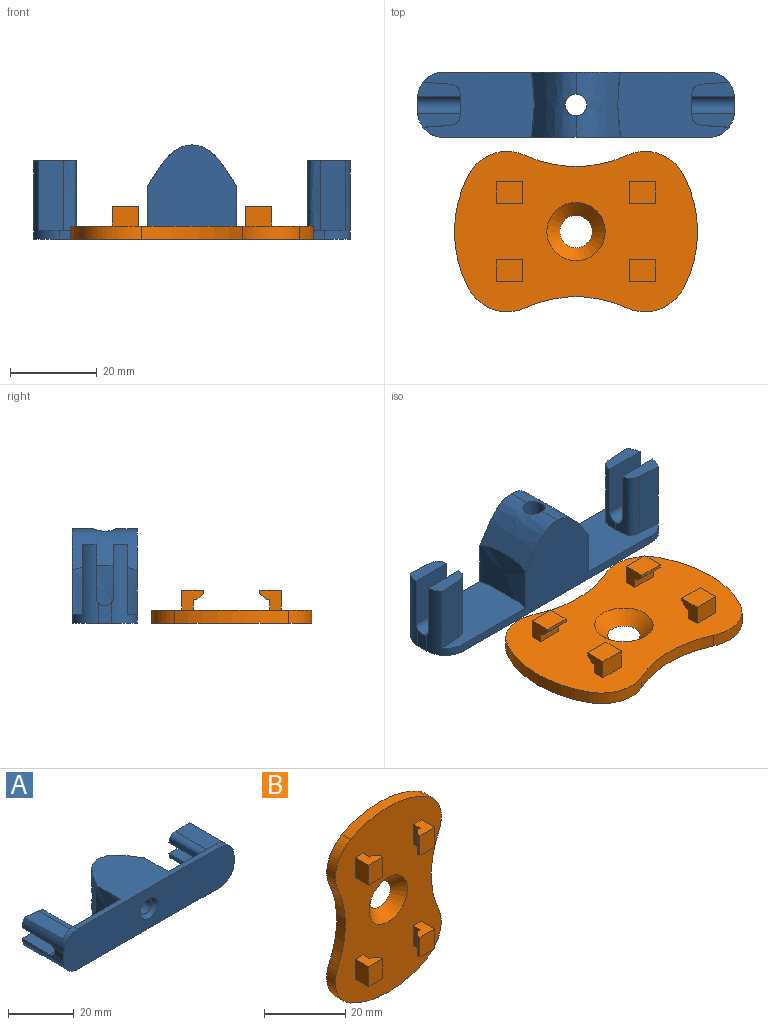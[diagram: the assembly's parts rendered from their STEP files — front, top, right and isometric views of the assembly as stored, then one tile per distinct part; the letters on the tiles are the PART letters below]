
ASSEMBLY  parts=2 mates=1
PART A: 35 faces, bbox 73x21.7x15 mm
  f0: plane 9.98x3.3mm, normal (0,1,0), area 26.2mm2, adj f14,f15,f26,f31
  f1: plane 9.98x3.3mm, normal (0,1,0), area 26.2mm2, adj f19,f20,f27,f29
  f2: extruded ~15x10.29mm, area 195.9mm2, adj f3,f7,f9,f22,f23
  f3: extruded ~15x10.29mm, area 195.9mm2, adj f2,f4,f7,f9,f23
  f4: extruded ~15x11.24mm, area 165.3mm2, adj f3,f5,f7,f9
  f5: plane 25.71x15mm, normal (0,1,0), area 293.2mm2, adj f4,f7,f9,f17,f18,f19,f20,f27
  f6: plane 4.68x3mm, normal (-1,0,0), area 12.6mm2, adj f10,f25,f26,f33
  f7: plane 61x21.71mm, normal (0,0,-1), area 460.3mm2, adj f2,f3,f4,f5,f10,f11,f22,f25
  f8: plane 4.68x3mm, normal (1,0,0), area 12.6mm2, adj f10,f27,f28,f34
  f9: plane 61x21.71mm, normal (0,0,1), area 461mm2, adj f2,f3,f4,f5,f10,f11,f22,f26
  f10: plane 73x15mm, normal (0,-1,0), area 1020.6mm2, adj f6,f7,f8,f9,f24,f25,f26,f27
  f11: plane 25.71x15mm, normal (0,1,0), area 293.2mm2, adj f7,f9,f12,f13,f14,f15,f22,f25
  f12: plane 16x5.75mm, normal (0.06,0,-1), area 92.2mm2, adj f11,f13,f16,f25
  f13: extruded ~16x4.79mm, area 77.9mm2, adj f11,f12,f14,f16,f32,f33
  f14: extruded ~16x4.79mm, area 77.9mm2, adj f0,f11,f13,f15,f31,f33
  f15: plane 16x5.75mm, normal (0.06,0,1), area 92.2mm2, adj f0,f11,f14,f26
  f16: plane 9.98x3.3mm, normal (0,1,0), area 26.2mm2, adj f12,f13,f25,f32
  f17: plane 16x5.75mm, normal (-0.06,0,1), area 92.2mm2, adj f5,f18,f21,f28
  f18: extruded ~16x4.79mm, area 77.9mm2, adj f5,f17,f19,f21,f30,f34
  f19: extruded ~16x4.79mm, area 77.9mm2, adj f1,f5,f18,f20,f29,f34
  f20: plane 16x5.75mm, normal (-0.06,0,-1), area 92.2mm2, adj f1,f5,f19,f27
  f21: plane 9.98x3.3mm, normal (0,1,0), area 26.2mm2, adj f17,f18,f28,f30
  f22: extruded ~15x11.24mm, area 165.3mm2, adj f2,f7,f9,f11
  f23: cylinder r=2.5mm len=20.49mm, axis (0,-1,0), area 317.3mm2, adj f2,f3,f24
  f24: cone r=2.5mm half-angle=45deg, axis (0,-1,0), area 33.7mm2, adj f10,f23
  f25: cylinder r=6mm len=18mm, axis (0,-1,0), area 75.5mm2, adj f6,f7,f10,f11,f12,f16,f32,f33
  f26: cylinder r=6mm len=18mm, axis (0,1,0), area 75.5mm2, adj f0,f6,f9,f10,f11,f15,f31,f33
  f27: cylinder r=6mm len=18mm, axis (0,-1,0), area 75.5mm2, adj f1,f5,f7,f8,f10,f20,f29,f34
  f28: cylinder r=6mm len=18mm, axis (0,1,0), area 75.5mm2, adj f5,f8,f9,f10,f17,f21,f30,f34
  f29: plane 12x9.88mm, normal (0,0,1), area 118.5mm2, adj f1,f19,f27,f34
  f30: plane 12x9.88mm, normal (0,0,-1), area 118.5mm2, adj f18,f21,f28,f34
  f31: plane 12x9.88mm, normal (0,0,-1), area 118.5mm2, adj f0,f14,f26,f33
  f32: plane 12x9.88mm, normal (0,0,1), area 118.5mm2, adj f13,f16,f25,f33
  f33: cylinder r=2mm len=10mm, axis (-1,0,0), area 62.5mm2, adj f6,f13,f14,f25,f26,f31,f32
  f34: cylinder r=2mm len=10mm, axis (1,0,0), area 62.5mm2, adj f8,f18,f19,f27,f28,f29,f30
PART B: 43 faces, bbox 37x7.6x56 mm
  f0: plane 6x2.36mm, normal (-1,0,0), area 14.2mm2, adj f4,f22,f24,f32
  f1: plane 6x2.36mm, normal (-1,0,0), area 14.2mm2, adj f4,f18,f20,f30
  f2: plane 6x2.36mm, normal (1,0,0), area 14.2mm2, adj f4,f14,f16,f28
  f3: plane 6x2.36mm, normal (1,0,0), area 14.2mm2, adj f4,f10,f11,f26
  f4: plane 56x36.95mm, normal (0,-1,0), area 1554.1mm2, adj f0,f1,f2,f3,f5,f6,f7,f8
  f5: cylinder r=28mm len=23.4mm, axis (0,-1,0), area 72.4mm2, adj f4,f9,f35,f38
  f6: cylinder r=28mm len=26.37mm, axis (0,-1,0), area 82.4mm2, adj f4,f9,f35,f36
  f7: cylinder r=28mm len=23.4mm, axis (0,-1,0), area 72.4mm2, adj f4,f9,f36,f37
  f8: cylinder r=28mm len=26.37mm, axis (0,-1,0), area 82.4mm2, adj f4,f9,f37,f38
  f9: plane 56x36.95mm, normal (0,1,0), area 1717.3mm2, adj f5,f6,f7,f8,f34,f35,f36,f37
  f10: plane 5x4.56mm, normal (0,0,-1), area 16.2mm2, adj f3,f4,f12,f13,f26,f27,f41
  f11: plane 5x4.56mm, normal (0,0,1), area 16.2mm2, adj f3,f4,f12,f13,f26,f27,f41
  f12: plane 6x4.56mm, normal (-1,0,0), area 27.4mm2, adj f4,f10,f11,f13
  f13: plane 6x5mm, normal (0,-1,0), area 30mm2, adj f10,f11,f12,f27
  f14: plane 5x4.56mm, normal (0,0,1), area 16.2mm2, adj f2,f4,f15,f17,f28,f29,f42
  f15: plane 6x4.56mm, normal (-1,0,0), area 27.4mm2, adj f4,f14,f16,f17
  f16: plane 5x4.56mm, normal (0,0,-1), area 16.2mm2, adj f2,f4,f15,f17,f28,f29,f42
  f17: plane 6x5mm, normal (0,-1,0), area 30mm2, adj f14,f15,f16,f29
  f18: plane 5x4.56mm, normal (0,0,-1), area 16.2mm2, adj f1,f4,f19,f21,f30,f31,f39
  f19: plane 6x4.56mm, normal (1,0,0), area 27.4mm2, adj f4,f18,f20,f21
  f20: plane 5x4.56mm, normal (0,0,1), area 16.2mm2, adj f1,f4,f19,f21,f30,f31,f39
  f21: plane 6x5mm, normal (0,-1,0), area 30mm2, adj f18,f19,f20,f31
  f22: plane 5x4.56mm, normal (0,0,-1), area 16.2mm2, adj f0,f4,f23,f25,f32,f33,f40
  f23: plane 6x4.56mm, normal (1,0,0), area 27.4mm2, adj f4,f22,f24,f25
  f24: plane 5x4.56mm, normal (0,0,1), area 16.2mm2, adj f0,f4,f23,f25,f32,f33,f40
  f25: plane 6x5mm, normal (0,-1,0), area 30mm2, adj f22,f23,f24,f33
  f26: plane 6x0.8mm, normal (0,1,0), area 4.8mm2, adj f3,f10,f11,f41
  f27: plane 6x0.7mm, normal (1,0,0), area 4.2mm2, adj f10,f11,f13,f41
  f28: plane 6x0.8mm, normal (0,1,0), area 4.8mm2, adj f2,f14,f16,f42
  f29: plane 6x0.7mm, normal (1,0,0), area 4.2mm2, adj f14,f16,f17,f42
  f30: plane 6x0.8mm, normal (0,1,0), area 4.8mm2, adj f1,f18,f20,f39
  f31: plane 6x0.7mm, normal (-1,0,0), area 4.2mm2, adj f18,f20,f21,f39
  f32: plane 6x0.8mm, normal (0,1,0), area 4.8mm2, adj f0,f22,f24,f40
  f33: plane 6x0.7mm, normal (-1,0,0), area 4.2mm2, adj f22,f24,f25,f40
  f34: cone r=2.5mm half-angle=45deg, axis (0,-1,0), area 139.2mm2, adj f4,f9
  f35: cylinder r=10mm len=13mm, axis (0,1,0), area 45.3mm2, adj f4,f5,f6,f9
  f36: cylinder r=10mm len=13mm, axis (0,1,0), area 45.3mm2, adj f4,f6,f7,f9
  f37: cylinder r=10mm len=13mm, axis (0,1,0), area 45.3mm2, adj f4,f7,f8,f9
  f38: cylinder r=10mm len=13mm, axis (0,1,0), area 45.3mm2, adj f4,f5,f8,f9
  f39: plane 6x1.5mm, normal (-0.71,0.71,0), area 12.7mm2, adj f18,f20,f30,f31
  f40: plane 6x1.5mm, normal (-0.71,0.71,0), area 12.7mm2, adj f22,f24,f32,f33
  f41: plane 6x1.5mm, normal (0.71,0.71,0), area 12.7mm2, adj f10,f11,f26,f27
  f42: plane 6x1.5mm, normal (0.71,0.71,0), area 12.7mm2, adj f14,f16,f28,f29
PLACE A rot(axis=(1,0,0),90deg) t=(0,0,-3)mm
PLACE B rot(axis=(-0.58,-0.58,0.58),120deg) t=(0,-29.2,3)mm
MATE planar A.f23 <-> B.f34  axis (0,0,-1) through (0,0,0)mm
